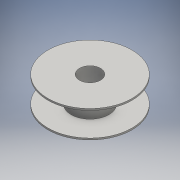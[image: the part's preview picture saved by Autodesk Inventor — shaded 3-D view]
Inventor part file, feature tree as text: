
AUTODESK INVENTOR PART (.ipt)
format: ipt  version: 2016 SP1 (Build 200210100, 210)  size: 110,080 bytes
history: native  units: mm
features: extrude x2, sketch x2, mirror x1
ambient origin geometry x8: Origin, YZ Plane, XZ Plane, XY Plane, X Axis, Y Axis, Z Axis, Center Point
bodies: Solid1 (feature_tree)
feature tree (5):
  extrude  "Extrusion1"  Depth=90.0mm
  extrude  "Extrusion2"  Depth=4.0mm
  mirror  "Mirror1"
  sketch  "Sketch1"  dims[d0=50.0mm d1=90.0mm]
  sketch  "Sketch2"  dims[d2=57.0mm d3=0.0mm d4=200.0mm d5=4.0mm d6=0.0mm]
